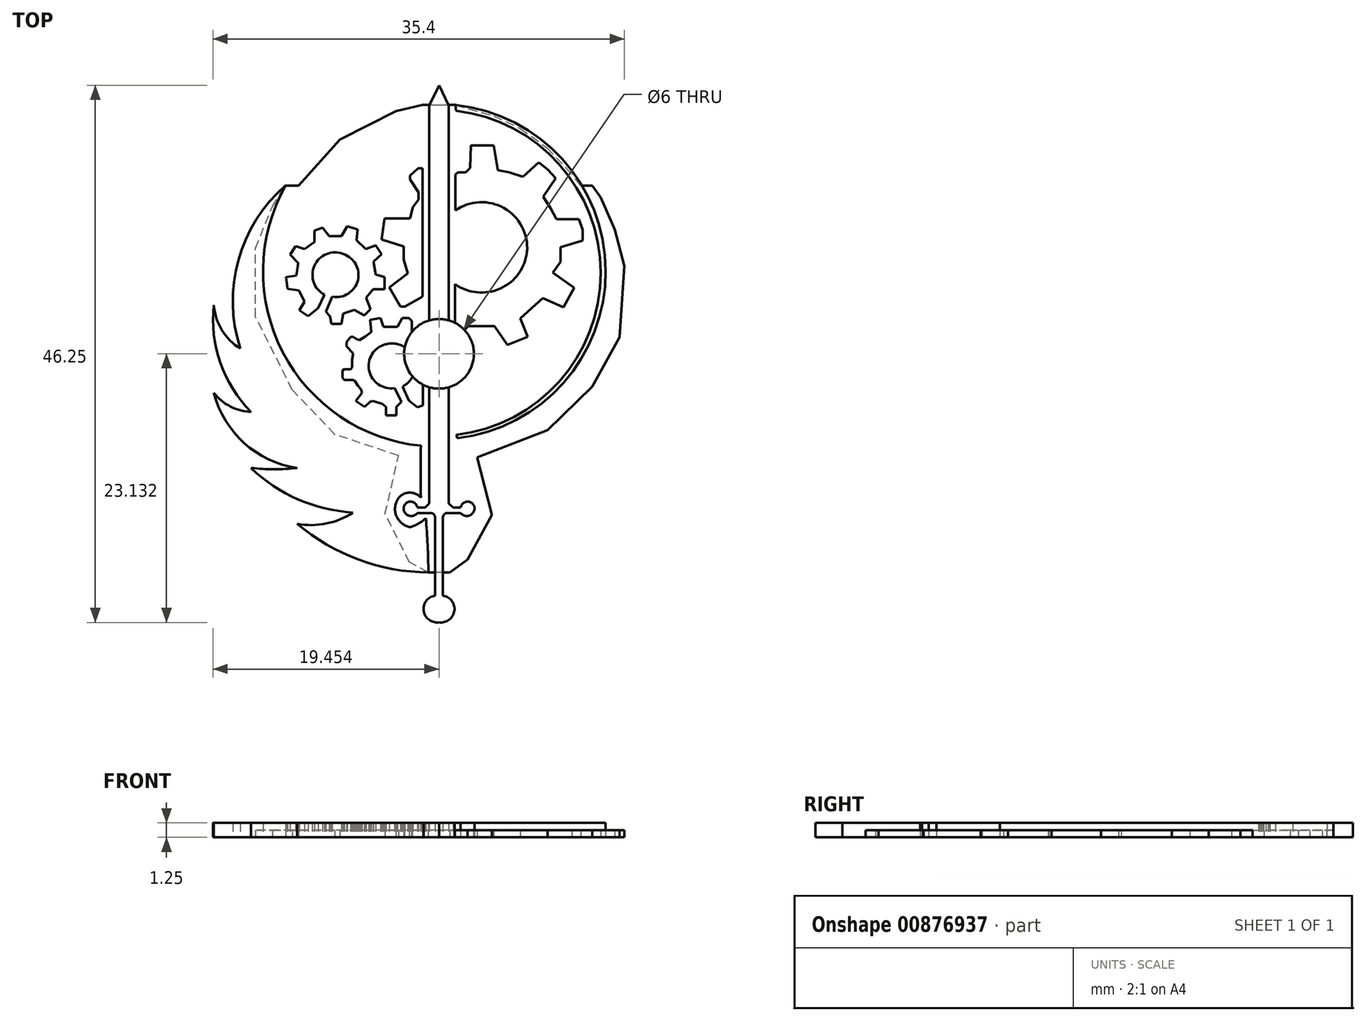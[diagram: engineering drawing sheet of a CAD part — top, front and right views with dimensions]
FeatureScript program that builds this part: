
annotation { "Feature Type Name" : "Feature", "Feature Type Description" : "" }
export const myFeature = defineFeature(function(context is Context, id is Id, definition is map)
    precondition{}
    {
        {
            var Q0;
            Q0=qCreatedBy(makeId("Top.planeOp"),FACE);
            var sketch = newSketch(context, id + "F0", { "sketchPlane" : qUnion([Q0])});
            skArc(sketch, "E0", {"start": v(-11.66, -15.08) * mm, "mid": v(-6.37, -18.16) * mm, "end": v(-0.36, -19.27) * mm});
            skArc(sketch, "E1", {"start": v(-11.66, -15.08) * mm, "mid": v(-9.16, -15.07) * mm, "end": v(-6.86, -14.11) * mm});
            skArc(sketch, "E2", {"start": v(-15.62, -10.28) * mm, "mid": v(-11.58, -12.97) * mm, "end": v(-6.86, -14.11) * mm});
            skArc(sketch, "E3", {"start": v(-18.83, -3.8) * mm, "mid": v(-16.22, -8.13) * mm, "end": v(-11.66, -10.28) * mm});
            skArc(sketch, "E4", {"start": v(-18.83, -3.8) * mm, "mid": v(-17.4, -4.98) * mm, "end": v(-15.62, -5.45) * mm});
            skArc(sketch, "E5", {"start": v(-18.83, 3.73) * mm, "mid": v(-18.27, -1.22) * mm, "end": v(-15.62, -5.45) * mm});
            skArc(sketch, "E6", {"start": v(-18.83, 3.73) * mm, "mid": v(-18.13, 1.6) * mm, "end": v(-16.54, 0) * mm});
            skArc(sketch, "E7", {"start": v(-12.64, 14.05) * mm, "mid": v(-16.72, 7.62) * mm, "end": v(-16.54, 0) * mm});
            skArc(sketch, "E8", {"start": v(-12.64, 14.05) * mm, "mid": v(-12.9, -0.3) * mm, "end": v(-1, -8.36) * mm});
            skArc(sketch, "E9", {"start": v(-1, -8.36) * mm, "mid": v(-1.04, -10.6) * mm, "end": v(-1, -12.84) * mm});
            skArc(sketch, "E10", {"start": v(-1, -12.84) * mm, "mid": v(-2.18, -12.42) * mm, "end": v(-3.13, -13.23) * mm});
            skArc(sketch, "E11", {"start": v(-3.13, -13.23) * mm, "mid": v(-3.03, -14.59) * mm, "end": v(-1.92, -15.37) * mm});
            skArc(sketch, "E12", {"start": v(-1.92, -15.37) * mm, "mid": v(-1.2, -15.07) * mm, "end": v(-0.59, -14.6) * mm});
            skArc(sketch, "E13", {"start": v(-0.36, -19.27) * mm, "mid": v(-0.43, -16.94) * mm, "end": v(-0.59, -14.6) * mm});
            skLineSegment(sketch, "E14", {"start": v(0.55, 22.67) * mm, "end": v(0.55, -23.56) * mm});
            skArc(sketch, "E15.MirrorCS", {"start": v(16.73, -10.28) * mm, "mid": v(12.69, -12.97) * mm, "end": v(7.97, -14.11) * mm});
            skArc(sketch, "E16.MirrorCS", {"start": v(19.94, -3.8) * mm, "mid": v(17.33, -8.13) * mm, "end": v(12.76, -10.28) * mm});
            skArc(sketch, "E17.MirrorCS", {"start": v(19.94, -3.8) * mm, "mid": v(18.52, -4.98) * mm, "end": v(16.73, -5.45) * mm});
            skArc(sketch, "E18.MirrorCS", {"start": v(2.11, -12.84) * mm, "mid": v(3.29, -12.42) * mm, "end": v(4.23, -13.23) * mm});
            skArc(sketch, "E19.MirrorCS", {"start": v(4.23, -13.23) * mm, "mid": v(4.14, -14.59) * mm, "end": v(3.03, -15.37) * mm});
            skArc(sketch, "E20.MirrorCS", {"start": v(13.75, 14.05) * mm, "mid": v(17.83, 7.62) * mm, "end": v(17.65, 0) * mm});
            skArc(sketch, "E21.MirrorCS", {"start": v(19.94, 3.73) * mm, "mid": v(19.38, -1.22) * mm, "end": v(16.73, -5.45) * mm});
            skArc(sketch, "E22.MirrorCS", {"start": v(19.94, 3.73) * mm, "mid": v(19.24, 1.6) * mm, "end": v(17.65, 0) * mm});
            skArc(sketch, "E23.MirrorCS", {"start": v(13.75, 14.05) * mm, "mid": v(14, -0.3) * mm, "end": v(2.11, -8.36) * mm});
            skArc(sketch, "E24.MirrorCS", {"start": v(12.76, -15.08) * mm, "mid": v(10.27, -15.07) * mm, "end": v(7.97, -14.11) * mm});
            skArc(sketch, "E25.MirrorCS", {"start": v(3.03, -15.37) * mm, "mid": v(2.32, -15.07) * mm, "end": v(1.7, -14.6) * mm});
            skArc(sketch, "E26.MirrorCS", {"start": v(12.76, -15.08) * mm, "mid": v(7.48, -18.16) * mm, "end": v(1.46, -19.27) * mm});
            skArc(sketch, "E27.MirrorCS", {"start": v(1.46, -19.27) * mm, "mid": v(1.53, -16.94) * mm, "end": v(1.7, -14.6) * mm});
            skArc(sketch, "E28", {"start": v(2.13, -7.72) * mm, "mid": v(14.9, 6.7) * mm, "end": v(1.97, 20.98) * mm});
            skArc(sketch, "E29", {"start": v(2.03, -7.42) * mm, "mid": v(14.46, 6.53) * mm, "end": v(2.02, 20.47) * mm});
            skArc(sketch, "E30", {"start": v(1.97, 20.98) * mm, "mid": v(2, 20.72) * mm, "end": v(2.02, 20.47) * mm});
            skArc(sketch, "E31", {"start": v(2.13, -7.72) * mm, "mid": v(2.08, -7.57) * mm, "end": v(2.03, -7.42) * mm});
            skArc(sketch, "E32.MirrorCS", {"start": v(-1.02, -7.72) * mm, "mid": v(-0.97, -7.57) * mm, "end": v(-0.92, -7.42) * mm});
            skArc(sketch, "E33.MirrorCS", {"start": v(-0.86, 20.98) * mm, "mid": v(-0.89, 20.72) * mm, "end": v(-0.91, 20.47) * mm});
            skArc(sketch, "E34.MirrorCS", {"start": v(-0.92, -7.42) * mm, "mid": v(-13.35, 6.53) * mm, "end": v(-0.91, 20.47) * mm});
            skArc(sketch, "E35.MirrorCS", {"start": v(-1.02, -7.72) * mm, "mid": v(-13.79, 6.7) * mm, "end": v(-0.86, 20.98) * mm});
            skLineSegment(sketch, "E36", {"start": v(0.55, 22.67) * mm, "end": v(-0.3, 20.93) * mm});
            skLineSegment(sketch, "E37", {"start": v(-0.3, -13.32) * mm, "end": v(-0.3, 20.93) * mm});
            skLineSegment(sketch, "E38", {"start": v(-0.3, -13.32) * mm, "end": v(-0.65, -13.7) * mm});
            skLineSegment(sketch, "E39", {"start": v(-0.65, -13.7) * mm, "end": v(-1.31, -13.7) * mm});
            skArc(sketch, "E40", {"start": v(-1.31, -13.7) * mm, "mid": v(-1.98, -13.18) * mm, "end": v(-2.5, -13.85) * mm});
            skArc(sketch, "E41", {"start": v(-2.5, -13.85) * mm, "mid": v(-2, -14.4) * mm, "end": v(-1.31, -14.15) * mm});
            skLineSegment(sketch, "E42", {"start": v(-1.31, -14.15) * mm, "end": v(-0.18, -14.15) * mm});
            skArc(sketch, "E43", {"start": v(0.21, -14.56) * mm, "mid": v(0.1, -14.27) * mm, "end": v(-0.18, -14.15) * mm});
            skLineSegment(sketch, "E44", {"start": v(0.21, -14.56) * mm, "end": v(0.21, -21.27) * mm});
            skArc(sketch, "E45", {"start": v(0.21, -21.27) * mm, "mid": v(-0.76, -22.59) * mm, "end": v(0.55, -23.56) * mm});
            skArc(sketch, "E46.MirrorCS", {"start": v(0.9, -21.27) * mm, "mid": v(1.87, -22.59) * mm, "end": v(0.55, -23.56) * mm});
            skLineSegment(sketch, "E47.MirrorCS", {"start": v(0.9, -14.56) * mm, "end": v(0.9, -21.27) * mm});
            skArc(sketch, "E48.MirrorCS", {"start": v(0.9, -14.56) * mm, "mid": v(1, -14.27) * mm, "end": v(1.29, -14.15) * mm});
            skLineSegment(sketch, "E49.MirrorCS", {"start": v(2.42, -14.15) * mm, "end": v(1.29, -14.15) * mm});
            skArc(sketch, "E50.MirrorCS", {"start": v(3.6, -13.85) * mm, "mid": v(3.1, -14.4) * mm, "end": v(2.42, -14.15) * mm});
            skLineSegment(sketch, "E51.MirrorCS", {"start": v(1.76, -13.7) * mm, "end": v(2.42, -13.7) * mm});
            skArc(sketch, "E52.MirrorCS", {"start": v(2.42, -13.7) * mm, "mid": v(3.09, -13.18) * mm, "end": v(3.6, -13.85) * mm});
            skLineSegment(sketch, "E53.MirrorCS", {"start": v(0.55, 22.67) * mm, "end": v(1.4, 20.93) * mm});
            skLineSegment(sketch, "E54.MirrorCS", {"start": v(1.4, -13.32) * mm, "end": v(1.4, 20.93) * mm});
            skLineSegment(sketch, "E55.MirrorCS", {"start": v(1.4, -13.32) * mm, "end": v(1.76, -13.7) * mm});
            skLineSegment(sketch, "E56", {"start": v(-3.29, -3.4) * mm, "end": v(-2.67, -4.56) * mm});
            skLineSegment(sketch, "E57", {"start": v(-2.67, -4.56) * mm, "end": v(-3.1, -5.02) * mm});
            skLineSegment(sketch, "E58", {"start": v(-3.1, -5.02) * mm, "end": v(-3.1, -5.74) * mm});
            skLineSegment(sketch, "E59", {"start": v(-3.1, -5.74) * mm, "end": v(-4, -5.74) * mm});
            skLineSegment(sketch, "E60", {"start": v(-4, -5.74) * mm, "end": v(-4, -5) * mm});
            skLineSegment(sketch, "E61", {"start": v(-4, -5) * mm, "end": v(-4.32, -4.77) * mm});
            skLineSegment(sketch, "E62", {"start": v(-4.32, -4.77) * mm, "end": v(-5.1, -4.52) * mm});
            skLineSegment(sketch, "E63", {"start": v(-5.1, -4.52) * mm, "end": v(-5.36, -4.57) * mm});
            skLineSegment(sketch, "E64", {"start": v(-5.36, -4.57) * mm, "end": v(-5.84, -5.01) * mm});
            skLineSegment(sketch, "E65", {"start": v(-5.84, -5.01) * mm, "end": v(-6.61, -4.5) * mm});
            skLineSegment(sketch, "E66", {"start": v(-6.61, -4.5) * mm, "end": v(-6.09, -3.8) * mm});
            skLineSegment(sketch, "E67", {"start": v(-6.09, -3.8) * mm, "end": v(-6.18, -3.5) * mm});
            skLineSegment(sketch, "E68", {"start": v(-6.18, -3.5) * mm, "end": v(-6.43, -3.21) * mm});
            skLineSegment(sketch, "E69", {"start": v(-6.43, -3.21) * mm, "end": v(-6.72, -2.76) * mm});
            skLineSegment(sketch, "E70", {"start": v(-6.72, -2.76) * mm, "end": v(-6.86, -2.68) * mm});
            skLineSegment(sketch, "E71", {"start": v(-6.86, -2.68) * mm, "end": v(-7.59, -2.68) * mm});
            skLineSegment(sketch, "E72", {"start": v(-7.59, -2.68) * mm, "end": v(-7.75, -2.52) * mm});
            skLineSegment(sketch, "E73", {"start": v(-7.75, -2.52) * mm, "end": v(-7.75, -1.88) * mm});
            skLineSegment(sketch, "E74", {"start": v(-7.75, -1.88) * mm, "end": v(-7.6, -1.78) * mm});
            skLineSegment(sketch, "E75", {"start": v(-7.6, -1.78) * mm, "end": v(-7.07, -1.78) * mm});
            skLineSegment(sketch, "E76", {"start": v(-7.07, -1.78) * mm, "end": v(-6.92, -1.6) * mm});
            skLineSegment(sketch, "E77", {"start": v(-6.92, -1.6) * mm, "end": v(-6.92, -0.94) * mm});
            skLineSegment(sketch, "E78", {"start": v(-6.92, -0.94) * mm, "end": v(-6.82, -0.4) * mm});
            skLineSegment(sketch, "E79", {"start": v(-6.82, -0.4) * mm, "end": v(-7.42, 0.18) * mm});
            skLineSegment(sketch, "E80", {"start": v(-7.42, 0.18) * mm, "end": v(-7.42, 0.4) * mm});
            skLineSegment(sketch, "E81", {"start": v(-7.42, 0.4) * mm, "end": v(-7.37, 0.62) * mm});
            skLineSegment(sketch, "E82", {"start": v(-7.37, 0.62) * mm, "end": v(-7.02, 1.01) * mm});
            skLineSegment(sketch, "E83", {"start": v(-7.02, 1.01) * mm, "end": v(-6.83, 1.01) * mm});
            skLineSegment(sketch, "E84", {"start": v(-6.83, 1.01) * mm, "end": v(-6.6, 0.87) * mm});
            skLineSegment(sketch, "E85", {"start": v(-6.6, 0.87) * mm, "end": v(-6.3, 0.74) * mm});
            skLineSegment(sketch, "E86", {"start": v(-6.3, 0.74) * mm, "end": v(-5.8, 1.06) * mm});
            skLineSegment(sketch, "E87", {"start": v(-5.8, 1.06) * mm, "end": v(-5.28, 1.41) * mm});
            skLineSegment(sketch, "E88", {"start": v(-5.28, 1.41) * mm, "end": v(-5.37, 2.47) * mm});
            skLineSegment(sketch, "E89", {"start": v(-5.37, 2.47) * mm, "end": v(-4.49, 2.65) * mm});
            skLineSegment(sketch, "E90", {"start": v(-4.49, 2.65) * mm, "end": v(-4.22, 1.89) * mm});
            skLineSegment(sketch, "E91", {"start": v(-4.22, 1.89) * mm, "end": v(-3.03, 1.89) * mm});
            skLineSegment(sketch, "E92", {"start": v(-3.03, 1.89) * mm, "end": v(-2.62, 2.64) * mm});
            skLineSegment(sketch, "E93", {"start": v(-2.62, 2.64) * mm, "end": v(-2.05, 2.64) * mm});
            skLineSegment(sketch, "E94", {"start": v(-2.05, 2.64) * mm, "end": v(-1.79, 2.39) * mm});
            skLineSegment(sketch, "E95", {"start": v(-1.79, 2.39) * mm, "end": v(-1.79, 1.45) * mm});
            skLineSegment(sketch, "E96", {"start": v(-1.79, 1.45) * mm, "end": v(-0.85, 0.61) * mm});
            skLineSegment(sketch, "E97", {"start": v(-0.85, 0.61) * mm, "end": v(-0.85, -3.53) * mm});
            skLineSegment(sketch, "E98", {"start": v(-0.85, -3.53) * mm, "end": v(-0.85, -4.88) * mm});
            skLineSegment(sketch, "E99", {"start": v(-0.85, -4.88) * mm, "end": v(-1.3, -5.04) * mm});
            skLineSegment(sketch, "E100", {"start": v(-1.3, -5.04) * mm, "end": v(-2.04, -4.46) * mm});
            skLineSegment(sketch, "E101", {"start": v(-2.04, -4.46) * mm, "end": v(-2.6, -3.27) * mm});
            skArc(sketch, "E102", {"start": v(-4.06, 0.37) * mm, "mid": v(-5.46, -1.88) * mm, "end": v(-3.29, -3.4) * mm});
            skArc(sketch, "E103", {"start": v(-2.6, -3.27) * mm, "mid": v(-1.67, -0.78) * mm, "end": v(-4.06, 0.37) * mm});
            skLineSegment(sketch, "E104", {"start": v(-9.31, 4.64) * mm, "end": v(-9.84, 3.49) * mm});
            skLineSegment(sketch, "E105", {"start": v(-9.84, 3.49) * mm, "end": v(-10.72, 2.8) * mm});
            skLineSegment(sketch, "E106", {"start": v(-10.72, 2.8) * mm, "end": v(-11.48, 3.31) * mm});
            skLineSegment(sketch, "E107", {"start": v(-11.48, 3.31) * mm, "end": v(-11.01, 4.03) * mm});
            skLineSegment(sketch, "E108", {"start": v(-11.01, 4.03) * mm, "end": v(-11.5, 5.02) * mm});
            skLineSegment(sketch, "E109", {"start": v(-11.5, 5.02) * mm, "end": v(-12.47, 5.15) * mm});
            skLineSegment(sketch, "E110", {"start": v(-12.47, 5.15) * mm, "end": v(-12.61, 6.16) * mm});
            skLineSegment(sketch, "E111", {"start": v(-12.61, 6.16) * mm, "end": v(-11.74, 6.28) * mm});
            skLineSegment(sketch, "E112", {"start": v(-11.74, 6.28) * mm, "end": v(-11.55, 7.35) * mm});
            skLineSegment(sketch, "E113", {"start": v(-11.55, 7.35) * mm, "end": v(-12.27, 8.1) * mm});
            skLineSegment(sketch, "E114", {"start": v(-12.27, 8.1) * mm, "end": v(-11.8, 8.83) * mm});
            skLineSegment(sketch, "E115", {"start": v(-11.8, 8.83) * mm, "end": v(-11.01, 8.59) * mm});
            skLineSegment(sketch, "E116", {"start": v(-11.01, 8.59) * mm, "end": v(-10.18, 9.19) * mm});
            skLineSegment(sketch, "E117", {"start": v(-10.18, 9.19) * mm, "end": v(-10.18, 10.15) * mm});
            skLineSegment(sketch, "E118", {"start": v(-10.18, 10.15) * mm, "end": v(-9.48, 10.42) * mm});
            skLineSegment(sketch, "E119", {"start": v(-9.48, 10.42) * mm, "end": v(-8.9, 9.68) * mm});
            skLineSegment(sketch, "E120", {"start": v(-8.9, 9.68) * mm, "end": v(-7.84, 9.68) * mm});
            skLineSegment(sketch, "E121", {"start": v(-7.84, 9.68) * mm, "end": v(-7.34, 10.53) * mm});
            skLineSegment(sketch, "E122", {"start": v(-7.34, 10.53) * mm, "end": v(-6.44, 10.26) * mm});
            skLineSegment(sketch, "E123", {"start": v(-6.44, 10.26) * mm, "end": v(-6.56, 9.33) * mm});
            skLineSegment(sketch, "E124", {"start": v(-6.56, 9.33) * mm, "end": v(-5.75, 8.59) * mm});
            skLineSegment(sketch, "E125", {"start": v(-5.75, 8.59) * mm, "end": v(-4.9, 8.88) * mm});
            skLineSegment(sketch, "E126", {"start": v(-4.9, 8.88) * mm, "end": v(-4.38, 8.14) * mm});
            skLineSegment(sketch, "E127", {"start": v(-4.38, 8.14) * mm, "end": v(-5.08, 7.5) * mm});
            skLineSegment(sketch, "E128", {"start": v(-5.08, 7.5) * mm, "end": v(-4.88, 6.4) * mm});
            skLineSegment(sketch, "E129", {"start": v(-4.88, 6.4) * mm, "end": v(-4.13, 6.14) * mm});
            skLineSegment(sketch, "E130", {"start": v(-4.13, 6.14) * mm, "end": v(-4.13, 5.12) * mm});
            skLineSegment(sketch, "E131", {"start": v(-4.13, 5.12) * mm, "end": v(-5.1, 5.12) * mm});
            skLineSegment(sketch, "E132", {"start": v(-5.1, 5.12) * mm, "end": v(-5.73, 4.37) * mm});
            skLineSegment(sketch, "E133", {"start": v(-5.73, 4.37) * mm, "end": v(-5.34, 3.38) * mm});
            skLineSegment(sketch, "E134", {"start": v(-5.34, 3.38) * mm, "end": v(-5.88, 2.84) * mm});
            skLineSegment(sketch, "E135", {"start": v(-5.88, 2.84) * mm, "end": v(-6.74, 3.35) * mm});
            skLineSegment(sketch, "E136", {"start": v(-6.74, 3.35) * mm, "end": v(-7.68, 3.03) * mm});
            skLineSegment(sketch, "E137", {"start": v(-7.68, 3.03) * mm, "end": v(-7.84, 2.13) * mm});
            skLineSegment(sketch, "E138", {"start": v(-7.84, 2.13) * mm, "end": v(-8.72, 2.13) * mm});
            skLineSegment(sketch, "E139", {"start": v(-8.72, 2.13) * mm, "end": v(-8.84, 2.8) * mm});
            skLineSegment(sketch, "E140", {"start": v(-8.84, 2.8) * mm, "end": v(-9.17, 3.18) * mm});
            skLineSegment(sketch, "E141", {"start": v(-9.17, 3.18) * mm, "end": v(-8.63, 4.48) * mm});
            skArc(sketch, "E142", {"start": v(-8.63, 4.48) * mm, "mid": v(-6.44, 5.88) * mm, "end": v(-7.71, 8.15) * mm});
            skArc(sketch, "E143", {"start": v(-7.71, 8.15) * mm, "mid": v(-10.17, 7.15) * mm, "end": v(-9.31, 4.64) * mm});
            skLineSegment(sketch, "E144", {"start": v(-0.86, 4.47) * mm, "end": v(-0.86, 15.52) * mm});
            skLineSegment(sketch, "E145", {"start": v(-0.86, 15.52) * mm, "end": v(-1.24, 15.52) * mm});
            skLineSegment(sketch, "E146", {"start": v(-1.24, 15.52) * mm, "end": v(-1.93, 14.9) * mm});
            skLineSegment(sketch, "E147", {"start": v(-1.93, 14.9) * mm, "end": v(-1.93, 14.56) * mm});
            skLineSegment(sketch, "E148", {"start": v(-1.93, 14.56) * mm, "end": v(-1.22, 13.48) * mm});
            skLineSegment(sketch, "E149", {"start": v(-1.22, 13.48) * mm, "end": v(-1.22, 12.83) * mm});
            skLineSegment(sketch, "E150", {"start": v(-1.22, 12.83) * mm, "end": v(-1.69, 12.2) * mm});
            skLineSegment(sketch, "E151", {"start": v(-1.69, 12.2) * mm, "end": v(-1.93, 11.2) * mm});
            skLineSegment(sketch, "E152", {"start": v(-1.93, 11.2) * mm, "end": v(-4.12, 11.2) * mm});
            skLineSegment(sketch, "E153", {"start": v(-4.12, 11.2) * mm, "end": v(-4.4, 9.4) * mm});
            skLineSegment(sketch, "E154", {"start": v(-4.4, 9.4) * mm, "end": v(-2.48, 8.8) * mm});
            skLineSegment(sketch, "E155", {"start": v(-2.48, 8.8) * mm, "end": v(-2.48, 7.65) * mm});
            skLineSegment(sketch, "E156", {"start": v(-2.48, 7.65) * mm, "end": v(-2.13, 6.5) * mm});
            skLineSegment(sketch, "E157", {"start": v(-2.13, 6.5) * mm, "end": v(-3.73, 5.27) * mm});
            skLineSegment(sketch, "E158", {"start": v(-3.73, 5.27) * mm, "end": v(-2.76, 3.62) * mm});
            skLineSegment(sketch, "E159", {"start": v(-2.76, 3.62) * mm, "end": v(-2.4, 3.62) * mm});
            skLineSegment(sketch, "E160", {"start": v(-2.4, 3.62) * mm, "end": v(-0.86, 4.47) * mm});
            skLineSegment(sketch, "E161", {"start": v(1.93, 5.55) * mm, "end": v(1.93, 0.43) * mm});
            skLineSegment(sketch, "E162", {"start": v(1.93, 0.43) * mm, "end": v(3.03, 1.95) * mm});
            skLineSegment(sketch, "E163", {"start": v(3.03, 1.95) * mm, "end": v(5.32, 1.95) * mm});
            skLineSegment(sketch, "E164", {"start": v(5.32, 1.95) * mm, "end": v(6.44, 0.33) * mm});
            skLineSegment(sketch, "E165", {"start": v(6.44, 0.33) * mm, "end": v(8.18, 1) * mm});
            skLineSegment(sketch, "E166", {"start": v(8.18, 1) * mm, "end": v(7.56, 2.62) * mm});
            skLineSegment(sketch, "E167", {"start": v(7.56, 2.62) * mm, "end": v(9.47, 4.34) * mm});
            skLineSegment(sketch, "E168", {"start": v(9.47, 4.34) * mm, "end": v(11.27, 3.57) * mm});
            skLineSegment(sketch, "E169", {"start": v(11.27, 3.57) * mm, "end": v(12.2, 5.23) * mm});
            skLineSegment(sketch, "E170", {"start": v(12.2, 5.23) * mm, "end": v(10.35, 6.55) * mm});
            skLineSegment(sketch, "E171", {"start": v(10.35, 6.55) * mm, "end": v(11, 7.46) * mm});
            skLineSegment(sketch, "E172", {"start": v(11, 7.46) * mm, "end": v(11, 8.72) * mm});
            skLineSegment(sketch, "E173", {"start": v(11, 8.72) * mm, "end": v(12.91, 9.3) * mm});
            skLineSegment(sketch, "E174", {"start": v(12.91, 9.3) * mm, "end": v(12.91, 10.24) * mm});
            skLineSegment(sketch, "E175", {"start": v(12.91, 10.24) * mm, "end": v(12.6, 11.13) * mm});
            skLineSegment(sketch, "E176", {"start": v(12.6, 11.13) * mm, "end": v(10.65, 11.13) * mm});
            skLineSegment(sketch, "E177", {"start": v(10.65, 11.13) * mm, "end": v(10.15, 12.11) * mm});
            skLineSegment(sketch, "E178", {"start": v(10.15, 12.11) * mm, "end": v(9.52, 13.07) * mm});
            skLineSegment(sketch, "E179", {"start": v(9.52, 13.07) * mm, "end": v(10.59, 14.67) * mm});
            skLineSegment(sketch, "E180", {"start": v(10.59, 14.67) * mm, "end": v(9.9, 15.44) * mm});
            skLineSegment(sketch, "E181", {"start": v(9.9, 15.44) * mm, "end": v(9.14, 16.03) * mm});
            skLineSegment(sketch, "E182", {"start": v(9.14, 16.03) * mm, "end": v(7.77, 14.8) * mm});
            skLineSegment(sketch, "E183", {"start": v(7.77, 14.8) * mm, "end": v(6.58, 15.18) * mm});
            skLineSegment(sketch, "E184", {"start": v(6.58, 15.18) * mm, "end": v(5.6, 15.37) * mm});
            skLineSegment(sketch, "E185", {"start": v(5.6, 15.37) * mm, "end": v(5.26, 17.5) * mm});
            skLineSegment(sketch, "E186", {"start": v(5.26, 17.5) * mm, "end": v(3.29, 17.5) * mm});
            skLineSegment(sketch, "E187", {"start": v(3.29, 17.5) * mm, "end": v(3.25, 15.55) * mm});
            skLineSegment(sketch, "E188", {"start": v(3.25, 15.55) * mm, "end": v(2.84, 15.18) * mm});
            skLineSegment(sketch, "E189", {"start": v(2.84, 15.18) * mm, "end": v(2.18, 15.2) * mm});
            skLineSegment(sketch, "E190", {"start": v(2.18, 15.2) * mm, "end": v(1.95, 14.99) * mm});
            skLineSegment(sketch, "E191", {"start": v(1.95, 14.99) * mm, "end": v(1.95, 11.9) * mm});
            skArc(sketch, "E192", {"start": v(8.13, 8.36) * mm, "mid": v(6.17, 12.09) * mm, "end": v(1.95, 11.9) * mm});
            skArc(sketch, "E193", {"start": v(1.93, 5.55) * mm, "mid": v(5.83, 5.18) * mm, "end": v(8.13, 8.36) * mm});
            skArc(sketch, "E194", {"start": v(-15.62, -10.28) * mm, "mid": v(-13.64, -10.38) * mm, "end": v(-11.66, -10.28) * mm});
            skArc(sketch, "E195", {"start": v(12.76, -10.28) * mm, "mid": v(14.75, -10.4) * mm, "end": v(16.73, -10.28) * mm});
            skLineSegment(sketch, "E196", {"start": v(2.11, -8.36) * mm, "end": v(2.11, -12.84) * mm});
            skLineSegment(sketch, "E197", {"start": v(0.55, 22.67) * mm, "end": v(0.55, -0.45) * mm});
            skSolve(sketch);
        }
        {
            var Q0;
            Q0=qCreatedBy(makeId("Top.planeOp"),FACE);
            var sketch = newSketch(context, id + "F1", { "sketchPlane" : qUnion([Q0])});
            skLineSegment(sketch, "E198", {"start": v(-0.86, 20.99) * mm, "end": v(1.97, 20.99) * mm});
            skLineSegment(sketch, "E199", {"start": v(1.97, 20.99) * mm, "end": v(5.25, 20.03) * mm});
            skLineSegment(sketch, "E200", {"start": v(5.25, 20.03) * mm, "end": v(7.56, 18.96) * mm});
            skLineSegment(sketch, "E201", {"start": v(7.56, 18.96) * mm, "end": v(9.85, 17.28) * mm});
            skLineSegment(sketch, "E202", {"start": v(9.85, 17.28) * mm, "end": v(11.99, 15.01) * mm});
            skLineSegment(sketch, "E203", {"start": v(13.75, 14.04) * mm, "end": v(12.75, 14.04) * mm});
            skLineSegment(sketch, "E204", {"start": v(12.75, 14.04) * mm, "end": v(11.99, 15.01) * mm});
            skLineSegment(sketch, "E205", {"start": v(13.75, 14.04) * mm, "end": v(14.46, 13) * mm});
            skLineSegment(sketch, "E206", {"start": v(14.46, 13) * mm, "end": v(15.69, 10.26) * mm});
            skLineSegment(sketch, "E207", {"start": v(15.69, 10.26) * mm, "end": v(16.5, 7.1) * mm});
            skLineSegment(sketch, "E208", {"start": v(16.5, 7.1) * mm, "end": v(16.1, 1) * mm});
            skPoint(sketch, "E208.endSnap0", {"position": v(16.1, 8.68) * mm});
            skLineSegment(sketch, "E209", {"start": v(16.1, 1) * mm, "end": v(13.75, -3.26) * mm});
            skLineSegment(sketch, "E210", {"start": v(13.75, -3.26) * mm, "end": v(9.89, -7.01) * mm});
            skLineSegment(sketch, "E211", {"start": v(9.89, -7.01) * mm, "end": v(3.84, -9.36) * mm});
            skLineSegment(sketch, "E212", {"start": v(3.84, -9.36) * mm, "end": v(5.1, -14.31) * mm});
            skLineSegment(sketch, "E213", {"start": v(5.1, -14.31) * mm, "end": v(3, -18.16) * mm});
            skLineSegment(sketch, "E214", {"start": v(3, -18.16) * mm, "end": v(1.47, -19.26) * mm});
            skLineSegment(sketch, "E215", {"start": v(1.47, -19.26) * mm, "end": v(-0.4, -19.26) * mm});
            skLineSegment(sketch, "E216", {"start": v(-0.4, -19.26) * mm, "end": v(-2, -18.39) * mm});
            skLineSegment(sketch, "E217", {"start": v(-2, -18.39) * mm, "end": v(-4.09, -14.23) * mm});
            skLineSegment(sketch, "E218", {"start": v(-4.09, -14.23) * mm, "end": v(-2.94, -9.21) * mm});
            skLineSegment(sketch, "E219", {"start": v(-2.94, -9.21) * mm, "end": v(-8.4, -7.38) * mm});
            skLineSegment(sketch, "E220", {"start": v(-8.4, -7.38) * mm, "end": v(-12.07, -3.55) * mm});
            skLineSegment(sketch, "E221", {"start": v(-12.07, -3.55) * mm, "end": v(-15.24, 2.74) * mm});
            skLineSegment(sketch, "E222", {"start": v(-15.24, 2.74) * mm, "end": v(-15.24, 8.63) * mm});
            skLineSegment(sketch, "E223", {"start": v(-15.24, 8.63) * mm, "end": v(-13.8, 12.23) * mm});
            skLineSegment(sketch, "E224", {"start": v(-13.8, 12.23) * mm, "end": v(-12.64, 14.05) * mm});
            skLineSegment(sketch, "E225", {"start": v(-12.64, 14.05) * mm, "end": v(-11.54, 14.04) * mm});
            skLineSegment(sketch, "E226", {"start": v(-11.54, 14.04) * mm, "end": v(-7.99, 17.99) * mm});
            skLineSegment(sketch, "E227", {"start": v(-7.99, 17.99) * mm, "end": v(-3.14, 20.43) * mm});
            skLineSegment(sketch, "E228", {"start": v(-3.14, 20.43) * mm, "end": v(-0.86, 20.99) * mm});
            skSolve(sketch);
        }
        {
            var Q0;
            Q0=makeQuery(id+"F0.imprint","IMPRINT",FACE,{"disambiguationData":[TD([[makeQuery(id+"F0.imprint","IMPRINT",EDGE,{"derivedFrom":sQuery(id+"F0.wireOp",EDGE,"E17.MirrorCS")}),1.0]])]});
            var Q1;
            Q1=makeQuery(id+"F0.imprint","IMPRINT",FACE,{"disambiguationData":[TD([[makeQuery(id+"F0.imprint","IMPRINT",EDGE,{"derivedFrom":sQuery(id+"F0.wireOp",EDGE,"E0")}),1.0]])]});
            var Q2;
            Q2=makeQuery(id+"F0.imprint","IMPRINT",FACE,{"disambiguationData":[TD([[makeQuery(id+"F0.imprint","IMPRINT",EDGE,{"derivedFrom":sQuery(id+"F0.wireOp",EDGE,"E56")}),-1.0]])]});
            var Q3;
            Q3=makeQuery(id+"F0.imprint","IMPRINT",FACE,{"disambiguationData":[TD([[makeQuery(id+"F0.imprint","IMPRINT",EDGE,{"derivedFrom":sQuery(id+"F0.wireOp",EDGE,"E104")}),-1.0]])]});
            var Q4;
            Q4=makeQuery(id+"F0.imprint","IMPRINT",FACE,{"disambiguationData":[TD([[makeQuery(id+"F0.imprint","IMPRINT",EDGE,{"derivedFrom":sQuery(id+"F0.wireOp",EDGE,"E161")}),1.0]])]});
            var Q5;
            Q5=makeQuery(id+"F0.imprint","IMPRINT",FACE,{"disambiguationData":[TD([[makeQuery(id+"F0.imprint","IMPRINT",EDGE,{"derivedFrom":sQuery(id+"F0.wireOp",EDGE,"E14")}),1.0]])]});
            var Q6;
            Q6=makeQuery(id+"F0.imprint","IMPRINT",FACE,{"disambiguationData":[TD([[makeQuery(id+"F0.imprint","IMPRINT",EDGE,{"derivedFrom":sQuery(id+"F0.wireOp",EDGE,"E14")}),-1.0]])]});
            var Q7;
            Q7=makeQuery(id+"F0.imprint","IMPRINT",FACE,{"disambiguationData":[TD([[makeQuery(id+"F0.imprint","IMPRINT",EDGE,{"derivedFrom":sQuery(id+"F0.wireOp",EDGE,"E144")}),1.0]])]});
            var Q8;
            Q8=makeQuery(id+"F0.imprint","IMPRINT",FACE,{"disambiguationData":[TD([[makeQuery(id+"F0.imprint","IMPRINT",EDGE,{"derivedFrom":sQuery(id+"F0.wireOp",EDGE,"E32.MirrorCS")}),1.0]])]});
            var Q9;
            Q9=makeQuery(id+"F0.imprint","IMPRINT",FACE,{"disambiguationData":[TD([[makeQuery(id+"F0.imprint","IMPRINT",EDGE,{"derivedFrom":sQuery(id+"F0.wireOp",EDGE,"E28")}),1.0]])]});
            extrude(context, id + "F2", {"entities" : qUnion([Q0, Q1, Q2, Q3, Q4, Q5, Q6, Q7, Q8, Q9]), "depth" : 1.25 * mm, "offsetDistance" : 25.4 * mm});
        }
        {
            var Q0;
            Q0=makeQuery(id+"F1.imprint","IMPRINT",FACE,{"disambiguationData":[TD([[makeQuery(id+"F1.imprint","IMPRINT",EDGE,{"derivedFrom":sQuery(id+"F1.wireOp",EDGE,"E198")}),-1.0]])]});
            extrude(context, id + "F3", {"entities" : qUnion([Q0]), "depth" : .625 * mm, "offsetDistance" : 25.4 * mm});
        }
        {
            var Q0;
            Q0=qCreatedBy(makeId("Top.planeOp"),FACE);
            cPlane(context, id + "F4", {"entities" : qUnion([Q0]), "cplaneType" : CPlaneType.OFFSET, "offset" : 1.52 * mm, "width" : 152.4 * mm, "height" : 152.4 * mm});
        }
        {
            var Q0;
            Q0=qCreatedBy(id+"F4.planeOp",FACE);
            var sketch = newSketch(context, id + "F5", { "sketchPlane" : qUnion([Q0])});
            skCircle(sketch, "E229", {"center": v(0.55, -0.45) * mm, "radius": 3 * mm});
            skSolve(sketch);
        }
        {
            var Q0;
            Q0=makeQuery(id+"F5.imprint","IMPRINT",FACE,{"disambiguationData":[TD([[makeQuery(id+"F5.imprint","IMPRINT",EDGE,{"derivedFrom":sQuery(id+"F5.wireOp",EDGE,"E229")}),1.0]])]});
            extrude(context, id + "F6", {"entities" : qUnion([Q0]), "operationType" : NewBodyOperationType.REMOVE, "oppositeDirection" : true, "depth" : 2.54 * mm, "offsetDistance" : 25.4 * mm});
        }
    });
